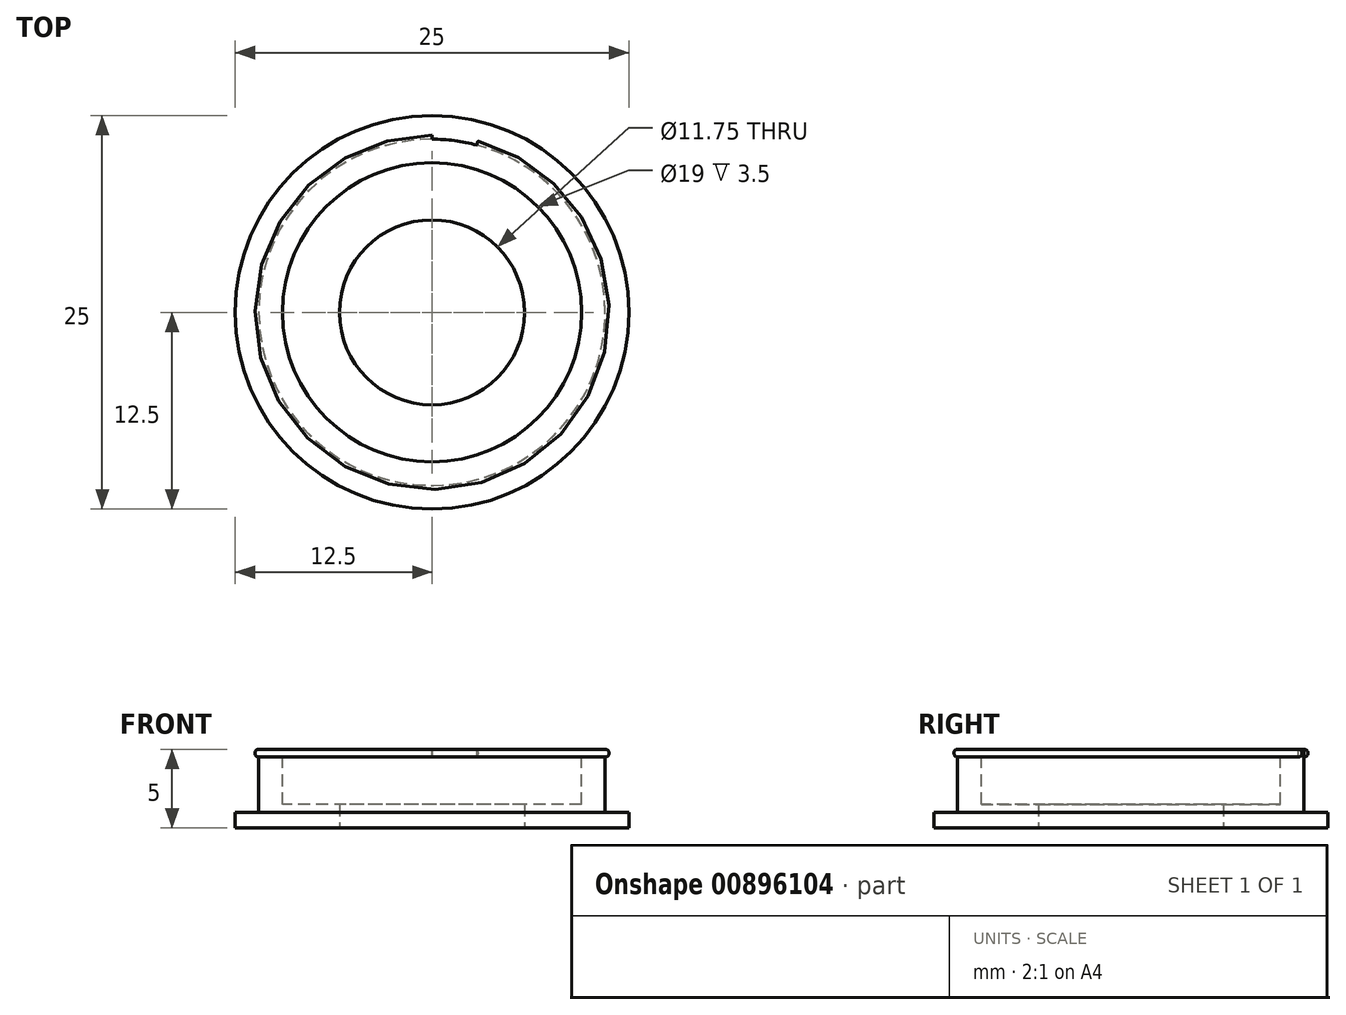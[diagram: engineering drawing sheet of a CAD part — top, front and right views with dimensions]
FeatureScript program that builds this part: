
annotation { "Feature Type Name" : "Feature", "Feature Type Description" : "" }
export const myFeature = defineFeature(function(context is Context, id is Id, definition is map)
    precondition{}
    {
        {
            var Q0;
            Q0=qCreatedBy(makeId("Top.planeOp"),FACE);
            var sketch = newSketch(context, id + "F0", { "sketchPlane" : qUnion([Q0])});
            skCircle(sketch, "E0", {"center": v(0, 0) * mm, "radius": 11 * mm});
            skCircle(sketch, "E1", {"center": v(0, 0) * mm, "radius": 5.88 * mm});
            skSolve(sketch);
        }
        {
            var Q0;
            Q0=makeQuery(id+"F0.imprint","IMPRINT",FACE,{"disambiguationData":[TD([[makeQuery(id+"F0.imprint","IMPRINT",EDGE,{"derivedFrom":sQuery(id+"F0.wireOp",EDGE,"E0")}),1.0]])]});
            extrude(context, id + "F1", {"entities" : qUnion([Q0]), "depth" : 5 * mm, "offsetDistance" : 25 * mm});
        }
        {
            var Q0;
            Q0=makeQuery(id+"F1.opExtrude","CAP_FACE",FACE,{"disambiguationData":[OSD([sQuery(id+"F0.wireOp",EDGE,"E0"),sQuery(id+"F0.wireOp",EDGE,"E1")])],"isStart":true});
            var sketch = newSketch(context, id + "F2", { "sketchPlane" : qUnion([Q0])});
            skCircle(sketch, "E2", {"center": v(0, 0) * mm, "radius": 12.5 * mm});
            skCircle(sketch, "E3", {"center": v(0, 0) * mm, "radius": 5.88 * mm});
            skSolve(sketch);
        }
        {
            var Q0;
            Q0=makeQuery(id+"F2.imprint","IMPRINT",FACE,{"disambiguationData":[TD([[makeQuery(id+"F2.imprint","IMPRINT",EDGE,{"derivedFrom":sQuery(id+"F2.wireOp",EDGE,"E2")}),1.0]])]});
            var Q1;
            Q1=makeQuery(id+"F2.imprint","IMPRINT",FACE,{"disambiguationData":[TD([[makeQuery(id+"F2.imprint","IMPRINT",EDGE,{"derivedFrom":sQuery(id+"F2.wireOp",EDGE,"E3")}),1.0]])]});
            extrude(context, id + "F3", {"entities" : qUnion([Q0, Q1]), "operationType" : NewBodyOperationType.ADD, "oppositeDirection" : true, "depth" : 1 * mm, "offsetDistance" : 25 * mm});
        }
        {
            var Q0;
            Q0=qCreatedBy(makeId("Right.planeOp"),FACE);
            var sketch = newSketch(context, id + "F4", { "sketchPlane" : qUnion([Q0])});
            skCircle(sketch, "E4", {"center": v(11, 4.75) * mm, "radius": 0.25 * mm});
            skLineSegment(sketch, "E5", {"start": v(0, 35.85) * mm, "end": v(0, -41.6) * mm, "construction": true});
            skSolve(sketch);
        }
        {
            var Q0;
            Q0=makeQuery(id+"F4.imprint","IMPRINT",FACE,{"disambiguationData":[TD([[makeQuery(id+"F4.imprint","IMPRINT",EDGE,{"derivedFrom":sQuery(id+"F4.wireOp",EDGE,"E4")}),1.0]])]});
            var Q1;
            Q1=sQuery(id+"F4.wireOp",EDGE,"E5");
            revolve(context, id + "F5", {"operationType" : NewBodyOperationType.ADD, "surfaceOperationType" : NewSurfaceOperationType.NEW, "entities" : qUnion([Q0]), "axis" : qUnion([Q1]), "revolveType" : RevolveType.FULL});
        }
        {
            var Q0;
            Q0=makeQuery(id+"F1.opExtrude","CAP_FACE",FACE,{"disambiguationData":[OSD([sQuery(id+"F0.wireOp",EDGE,"E0"),sQuery(id+"F0.wireOp",EDGE,"E1")])],"isStart":false});
            var sketch = newSketch(context, id + "F6", { "sketchPlane" : qUnion([Q0])});
            skArc(sketch, "E6", {"start": v(0, 11) * mm, "mid": v(1.44, 10.9) * mm, "end": v(2.85, 10.63) * mm});
            skArc(sketch, "E7", {"start": v(0, 12.5) * mm, "mid": v(1.63, 12.4) * mm, "end": v(3.24, 12.07) * mm});
            skLineSegment(sketch, "E8", {"start": v(0, 12.5) * mm, "end": v(0, 11) * mm});
            skLineSegment(sketch, "E9", {"start": v(3.24, 12.07) * mm, "end": v(2.85, 10.63) * mm});
            skLineSegment(sketch, "E10", {"start": v(0, 0) * mm, "end": v(2.85, 10.63) * mm, "construction": true});
            skArc(sketch, "E11.1.0", {"start": v(-5.08, 11.42) * mm, "mid": v(-3.55, 11.99) * mm, "end": v(-1.96, 12.35) * mm});
            skArc(sketch, "E11.1.1", {"start": v(-4.47, 10.05) * mm, "mid": v(-3.12, 10.55) * mm, "end": v(-1.72, 10.86) * mm});
            skLineSegment(sketch, "E11.1.2", {"start": v(-5.08, 11.42) * mm, "end": v(-4.47, 10.05) * mm});
            skLineSegment(sketch, "E11.1.3", {"start": v(-1.96, 12.35) * mm, "end": v(-1.72, 10.86) * mm});
            skArc(sketch, "E11.2.0", {"start": v(-9.29, 8.36) * mm, "mid": v(-8.12, 9.5) * mm, "end": v(-6.8, 10.48) * mm});
            skArc(sketch, "E11.2.1", {"start": v(-8.17, 7.36) * mm, "mid": v(-7.14, 8.36) * mm, "end": v(-6, 9.23) * mm});
            skLineSegment(sketch, "E11.2.2", {"start": v(-9.29, 8.36) * mm, "end": v(-8.17, 7.36) * mm});
            skLineSegment(sketch, "E11.2.3", {"start": v(-6.8, 10.48) * mm, "end": v(-6, 9.23) * mm});
            skArc(sketch, "E11.3.0", {"start": v(-11.89, 3.86) * mm, "mid": v(-11.28, 5.38) * mm, "end": v(-10.48, 6.8) * mm});
            skArc(sketch, "E11.3.1", {"start": v(-10.46, 3.4) * mm, "mid": v(-9.93, 4.74) * mm, "end": v(-9.23, 6) * mm});
            skLineSegment(sketch, "E11.3.2", {"start": v(-11.89, 3.86) * mm, "end": v(-10.46, 3.4) * mm});
            skLineSegment(sketch, "E11.3.3", {"start": v(-10.48, 6.8) * mm, "end": v(-9.23, 6) * mm});
            skArc(sketch, "E11.4.0", {"start": v(-12.43, -1.3) * mm, "mid": v(-12.5, 0.33) * mm, "end": v(-12.35, 1.96) * mm});
            skArc(sketch, "E11.4.1", {"start": v(-10.94, -1.15) * mm, "mid": v(-11, 0.29) * mm, "end": v(-10.86, 1.72) * mm});
            skLineSegment(sketch, "E11.4.2", {"start": v(-12.43, -1.3) * mm, "end": v(-10.94, -1.15) * mm});
            skLineSegment(sketch, "E11.4.3", {"start": v(-12.35, 1.96) * mm, "end": v(-10.86, 1.72) * mm});
            skArc(sketch, "E11.5.0", {"start": v(-10.83, -6.25) * mm, "mid": v(-11.55, -4.78) * mm, "end": v(-12.07, -3.24) * mm});
            skArc(sketch, "E11.5.1", {"start": v(-9.53, -5.5) * mm, "mid": v(-10.16, -4.2) * mm, "end": v(-10.63, -2.85) * mm});
            skLineSegment(sketch, "E11.5.2", {"start": v(-10.83, -6.25) * mm, "end": v(-9.53, -5.5) * mm});
            skLineSegment(sketch, "E11.5.3", {"start": v(-12.07, -3.24) * mm, "end": v(-10.63, -2.85) * mm});
            skArc(sketch, "E11.6.0", {"start": v(-7.35, -10.11) * mm, "mid": v(-8.6, -9.07) * mm, "end": v(-9.71, -7.87) * mm});
            skArc(sketch, "E11.6.1", {"start": v(-6.47, -8.9) * mm, "mid": v(-7.57, -7.98) * mm, "end": v(-8.55, -6.92) * mm});
            skLineSegment(sketch, "E11.6.2", {"start": v(-7.35, -10.11) * mm, "end": v(-6.47, -8.9) * mm});
            skLineSegment(sketch, "E11.6.3", {"start": v(-9.71, -7.87) * mm, "end": v(-8.55, -6.92) * mm});
            skArc(sketch, "E11.7.0", {"start": v(-2.6, -12.23) * mm, "mid": v(-4.17, -11.78) * mm, "end": v(-5.67, -11.14) * mm});
            skArc(sketch, "E11.7.1", {"start": v(-2.29, -10.76) * mm, "mid": v(-3.67, -10.37) * mm, "end": v(-5, -9.8) * mm});
            skLineSegment(sketch, "E11.7.2", {"start": v(-2.6, -12.23) * mm, "end": v(-2.29, -10.76) * mm});
            skLineSegment(sketch, "E11.7.3", {"start": v(-5.67, -11.14) * mm, "end": v(-5, -9.8) * mm});
            skArc(sketch, "E11.8.0", {"start": v(2.6, -12.23) * mm, "mid": v(0.98, -12.46) * mm, "end": v(-0.65, -12.48) * mm});
            skArc(sketch, "E11.8.1", {"start": v(2.29, -10.76) * mm, "mid": v(0.86, -10.97) * mm, "end": v(-0.58, -10.98) * mm});
            skLineSegment(sketch, "E11.8.2", {"start": v(2.6, -12.23) * mm, "end": v(2.29, -10.76) * mm});
            skLineSegment(sketch, "E11.8.3", {"start": v(-0.65, -12.48) * mm, "end": v(-0.58, -10.98) * mm});
            skArc(sketch, "E11.9.0", {"start": v(7.35, -10.11) * mm, "mid": v(5.96, -10.99) * mm, "end": v(4.48, -11.67) * mm});
            skArc(sketch, "E11.9.1", {"start": v(6.47, -8.9) * mm, "mid": v(5.25, -9.67) * mm, "end": v(3.94, -10.27) * mm});
            skLineSegment(sketch, "E11.9.2", {"start": v(7.35, -10.11) * mm, "end": v(6.47, -8.9) * mm});
            skLineSegment(sketch, "E11.9.3", {"start": v(4.48, -11.67) * mm, "end": v(3.94, -10.27) * mm});
            skArc(sketch, "E11.10.0", {"start": v(10.83, -6.25) * mm, "mid": v(9.92, -7.6) * mm, "end": v(8.84, -8.84) * mm});
            skArc(sketch, "E11.10.1", {"start": v(9.53, -5.5) * mm, "mid": v(8.73, -6.7) * mm, "end": v(7.78, -7.78) * mm});
            skLineSegment(sketch, "E11.10.2", {"start": v(10.83, -6.25) * mm, "end": v(9.53, -5.5) * mm});
            skLineSegment(sketch, "E11.10.3", {"start": v(8.84, -8.84) * mm, "end": v(7.78, -7.78) * mm});
            skArc(sketch, "E11.11.0", {"start": v(12.43, -1.3) * mm, "mid": v(12.15, -2.92) * mm, "end": v(11.67, -4.48) * mm});
            skArc(sketch, "E11.11.1", {"start": v(10.94, -1.15) * mm, "mid": v(10.7, -2.57) * mm, "end": v(10.27, -3.94) * mm});
            skLineSegment(sketch, "E11.11.2", {"start": v(12.43, -1.3) * mm, "end": v(10.94, -1.15) * mm});
            skLineSegment(sketch, "E11.11.3", {"start": v(11.67, -4.48) * mm, "end": v(10.27, -3.94) * mm});
            skArc(sketch, "E11.12.0", {"start": v(11.89, 3.86) * mm, "mid": v(12.3, 2.28) * mm, "end": v(12.48, 0.65) * mm});
            skArc(sketch, "E11.12.1", {"start": v(10.46, 3.4) * mm, "mid": v(10.82, 2) * mm, "end": v(10.98, 0.58) * mm});
            skLineSegment(sketch, "E11.12.2", {"start": v(11.89, 3.86) * mm, "end": v(10.46, 3.4) * mm});
            skLineSegment(sketch, "E11.12.3", {"start": v(12.48, 0.65) * mm, "end": v(10.98, 0.58) * mm});
            skArc(sketch, "E11.13.0", {"start": v(9.29, 8.36) * mm, "mid": v(10.3, 7.08) * mm, "end": v(11.14, 5.67) * mm});
            skArc(sketch, "E11.13.1", {"start": v(8.17, 7.36) * mm, "mid": v(9.07, 6.23) * mm, "end": v(9.8, 5) * mm});
            skLineSegment(sketch, "E11.13.2", {"start": v(9.29, 8.36) * mm, "end": v(8.17, 7.36) * mm});
            skLineSegment(sketch, "E11.13.3", {"start": v(11.14, 5.67) * mm, "end": v(9.8, 5) * mm});
            skArc(sketch, "E11.14.0", {"start": v(5.08, 11.42) * mm, "mid": v(6.53, 10.66) * mm, "end": v(7.87, 9.71) * mm});
            skArc(sketch, "E11.14.1", {"start": v(4.47, 10.05) * mm, "mid": v(5.75, 9.38) * mm, "end": v(6.92, 8.55) * mm});
            skLineSegment(sketch, "E11.14.2", {"start": v(5.08, 11.42) * mm, "end": v(4.47, 10.05) * mm});
            skLineSegment(sketch, "E11.14.3", {"start": v(7.87, 9.71) * mm, "end": v(6.92, 8.55) * mm});
            skSolve(sketch);
        }
        {
            var Q0;
            Q0=makeQuery(id+"F6.imprint","IMPRINT",FACE,{"disambiguationData":[TD([[makeQuery(id+"F6.imprint","IMPRINT",EDGE,{"derivedFrom":sQuery(id+"F6.wireOp",EDGE,"E11.2.0")}),-1.0]])]});
            var Q1;
            Q1=makeQuery(id+"F6.imprint","IMPRINT",FACE,{"disambiguationData":[TD([[makeQuery(id+"F6.imprint","IMPRINT",EDGE,{"derivedFrom":sQuery(id+"F6.wireOp",EDGE,"E11.1.0")}),-1.0]])]});
            var Q2;
            Q2=makeQuery(id+"F6.imprint","IMPRINT",FACE,{"disambiguationData":[TD([[makeQuery(id+"F6.imprint","IMPRINT",EDGE,{"derivedFrom":sQuery(id+"F6.wireOp",EDGE,"E6")}),1.0]])]});
            var Q3;
            Q3=makeQuery(id+"F6.imprint","IMPRINT",FACE,{"disambiguationData":[TD([[makeQuery(id+"F6.imprint","IMPRINT",EDGE,{"derivedFrom":sQuery(id+"F6.wireOp",EDGE,"E11.14.0")}),-1.0]])]});
            var Q4;
            Q4=makeQuery(id+"F6.imprint","IMPRINT",FACE,{"disambiguationData":[TD([[makeQuery(id+"F6.imprint","IMPRINT",EDGE,{"derivedFrom":sQuery(id+"F6.wireOp",EDGE,"E11.13.0")}),-1.0]])]});
            var Q5;
            Q5=makeQuery(id+"F6.imprint","IMPRINT",FACE,{"disambiguationData":[TD([[makeQuery(id+"F6.imprint","IMPRINT",EDGE,{"derivedFrom":sQuery(id+"F6.wireOp",EDGE,"E11.12.0")}),-1.0]])]});
            var Q6;
            Q6=makeQuery(id+"F6.imprint","IMPRINT",FACE,{"disambiguationData":[TD([[makeQuery(id+"F6.imprint","IMPRINT",EDGE,{"derivedFrom":sQuery(id+"F6.wireOp",EDGE,"E11.11.0")}),-1.0]])]});
            var Q7;
            Q7=makeQuery(id+"F6.imprint","IMPRINT",FACE,{"disambiguationData":[TD([[makeQuery(id+"F6.imprint","IMPRINT",EDGE,{"derivedFrom":sQuery(id+"F6.wireOp",EDGE,"E11.10.0")}),-1.0]])]});
            var Q8;
            Q8=makeQuery(id+"F6.imprint","IMPRINT",FACE,{"disambiguationData":[TD([[makeQuery(id+"F6.imprint","IMPRINT",EDGE,{"derivedFrom":sQuery(id+"F6.wireOp",EDGE,"E11.9.0")}),-1.0]])]});
            var Q9;
            Q9=makeQuery(id+"F6.imprint","IMPRINT",FACE,{"disambiguationData":[TD([[makeQuery(id+"F6.imprint","IMPRINT",EDGE,{"derivedFrom":sQuery(id+"F6.wireOp",EDGE,"E11.8.0")}),-1.0]])]});
            var Q10;
            Q10=makeQuery(id+"F6.imprint","IMPRINT",FACE,{"disambiguationData":[TD([[makeQuery(id+"F6.imprint","IMPRINT",EDGE,{"derivedFrom":sQuery(id+"F6.wireOp",EDGE,"E11.7.0")}),-1.0]])]});
            var Q11;
            Q11=makeQuery(id+"F6.imprint","IMPRINT",FACE,{"disambiguationData":[TD([[makeQuery(id+"F6.imprint","IMPRINT",EDGE,{"derivedFrom":sQuery(id+"F6.wireOp",EDGE,"E11.6.0")}),-1.0]])]});
            var Q12;
            Q12=makeQuery(id+"F6.imprint","IMPRINT",FACE,{"disambiguationData":[TD([[makeQuery(id+"F6.imprint","IMPRINT",EDGE,{"derivedFrom":sQuery(id+"F6.wireOp",EDGE,"E11.5.0")}),-1.0]])]});
            var Q13;
            Q13=makeQuery(id+"F6.imprint","IMPRINT",FACE,{"disambiguationData":[TD([[makeQuery(id+"F6.imprint","IMPRINT",EDGE,{"derivedFrom":sQuery(id+"F6.wireOp",EDGE,"E11.4.0")}),-1.0]])]});
            var Q14;
            Q14=makeQuery(id+"F6.imprint","IMPRINT",FACE,{"disambiguationData":[TD([[makeQuery(id+"F6.imprint","IMPRINT",EDGE,{"derivedFrom":sQuery(id+"F6.wireOp",EDGE,"E11.3.0")}),-1.0]])]});
            extrude(context, id + "F7", {"entities" : qUnion([Q0, Q1, Q2, Q3, Q4, Q5, Q6, Q7, Q8, Q9, Q10, Q11, Q12, Q13, Q14]), "operationType" : NewBodyOperationType.REMOVE, "endBound" : BoundingType.UP_TO_NEXT, "oppositeDirection" : true, "depth" : 25 * mm, "offsetDistance" : 25 * mm});
        }
        {
            var Q0;
            Q0=makeQuery(id+"F1.opExtrude","CAP_FACE",FACE,{"disambiguationData":[OSD([sQuery(id+"F0.wireOp",EDGE,"E0"),sQuery(id+"F0.wireOp",EDGE,"E1")])],"isStart":false});
            var sketch = newSketch(context, id + "F8", { "sketchPlane" : qUnion([Q0])});
            skCircle(sketch, "E12", {"center": v(0, 0) * mm, "radius": 9.5 * mm});
            skSolve(sketch);
        }
        {
            var Q0;
            Q0 = qSketchRegion(id + "F8", true);
            extrude(context, id + "F9", {"entities" : qUnion([Q0]), "operationType" : NewBodyOperationType.REMOVE, "oppositeDirection" : true, "depth" : 3.5 * mm, "offsetDistance" : 25 * mm});
        }
    });
